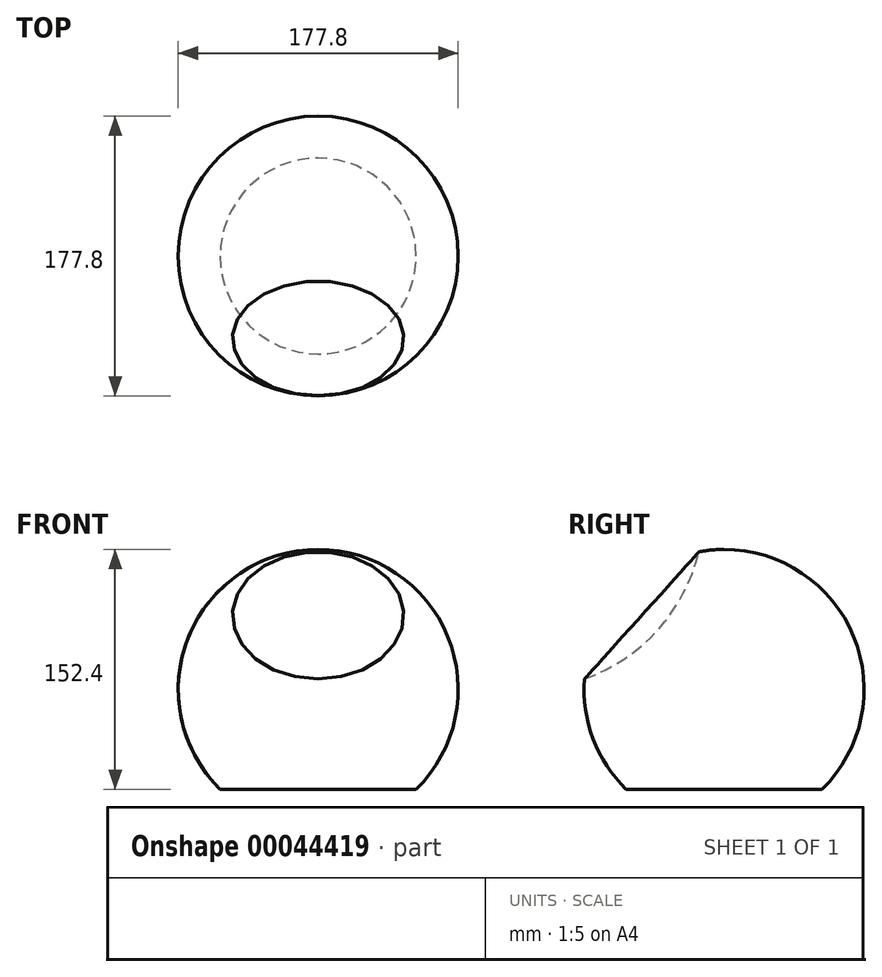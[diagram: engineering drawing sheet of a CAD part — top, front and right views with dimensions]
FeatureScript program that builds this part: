
annotation { "Feature Type Name" : "Feature", "Feature Type Description" : "" }
export const myFeature = defineFeature(function(context is Context, id is Id, definition is map)
    precondition{}
    {
        {
            var Q0;
            Q0=qCreatedBy(makeId("Front.planeOp"),FACE);
            var sketch = newSketch(context, id + "F0", { "sketchPlane" : qUnion([Q0])});
            skArc(sketch, "E0", {"start": v(0, -88.9) * mm, "mid": v(88.9, 0) * mm, "end": v(0, 88.9) * mm});
            skLineSegment(sketch, "E1", {"start": v(0, 0) * mm, "end": v(0, 126.5) * mm});
            skLineSegment(sketch, "E2", {"start": v(0, 0) * mm, "end": v(0, -102.91) * mm});
            skSolve(sketch);
        }
        {
            var Q0;
            {var subQ3=sQuery(id+"F0.wireOp",EDGE,"E0");Q0=makeQuery(id+"F0.imprint","IMPRINT",FACE,{"disambiguationData":[TD([[makeQuery(id+"F0.imprint","IMPRINT",EDGE,{"derivedFrom":subQ3}),1.0]])]});}
            var Q1;
            Q1=sQuery(id+"F0.wireOp",EDGE,"E1");
            revolve(context, id + "F1", {"entities" : qUnion([Q0]), "axis" : qUnion([Q1]), "revolveType" : RevolveType.FULL});
        }
        {
            var Q0;
            Q0=qCreatedBy(makeId("Top.planeOp"),FACE);
            cPlane(context, id + "F2", {"entities" : qUnion([Q0]), "cplaneType" : CPlaneType.OFFSET, "offset" : 63.5 * mm, "oppositeDirection" : true, "width" : 152.4 * mm, "height" : 152.4 * mm});
        }
        {
            var Q0;
            Q0=qCreatedBy(id+"F2.planeOp",FACE);
            var sketch = newSketch(context, id + "F3", { "sketchPlane" : qUnion([Q0])});
            skCircle(sketch, "E3", {"center": v(0, 0) * mm, "radius": 283.32 * mm});
            skSolve(sketch);
        }
        {
            var Q0;
            Q0=makeQuery(id+"F3.imprint","IMPRINT",FACE,{"disambiguationData":[TD([[makeQuery(id+"F3.imprint","IMPRINT",EDGE,{"derivedFrom":sQuery(id+"F3.wireOp",EDGE,"E3")}),1.0]])]});
            extrude(context, id + "F4", {"entities" : qUnion([Q0]), "operationType" : NewBodyOperationType.REMOVE, "oppositeDirection" : true, "depth" : 25.4 * mm});
        }
        {
            var Q0;
            Q0=qCreatedBy(makeId("Right.planeOp"),FACE);
            var sketch = newSketch(context, id + "F5", { "sketchPlane" : qUnion([Q0])});
            skLineSegment(sketch, "E4", {"start": v(0, 0) * mm, "end": v(0, 114.3) * mm, "construction": true});
            skLineSegment(sketch, "E5", {"start": v(0, 114.3) * mm, "end": v(-127, 114.3) * mm, "construction": true});
            skLineSegment(sketch, "E6", {"start": v(-127, 114.3) * mm, "end": v(-127, 228.6) * mm, "construction": true});
            skLineSegment(sketch, "E7", {"start": v(-127, 228.6) * mm, "end": v(-127, 0) * mm});
            skArc(sketch, "E8", {"start": v(-127, 0) * mm, "mid": v(-12.7, 114.3) * mm, "end": v(-127, 228.6) * mm});
            skSolve(sketch);
        }
        {
            var Q0;
            Q0=makeQuery(id+"F5.imprint","IMPRINT",FACE,{"disambiguationData":[TD([[makeQuery(id+"F5.imprint","IMPRINT",EDGE,{"derivedFrom":sQuery(id+"F5.wireOp",EDGE,"E7")}),1.0]])]});
            var Q1;
            Q1=sQuery(id+"F5.wireOp",EDGE,"E7");
            revolve(context, id + "F6", {"operationType" : NewBodyOperationType.REMOVE, "entities" : qUnion([Q0]), "axis" : qUnion([Q1]), "revolveType" : RevolveType.FULL, "oppositeDirection" : true});
        }
    });
